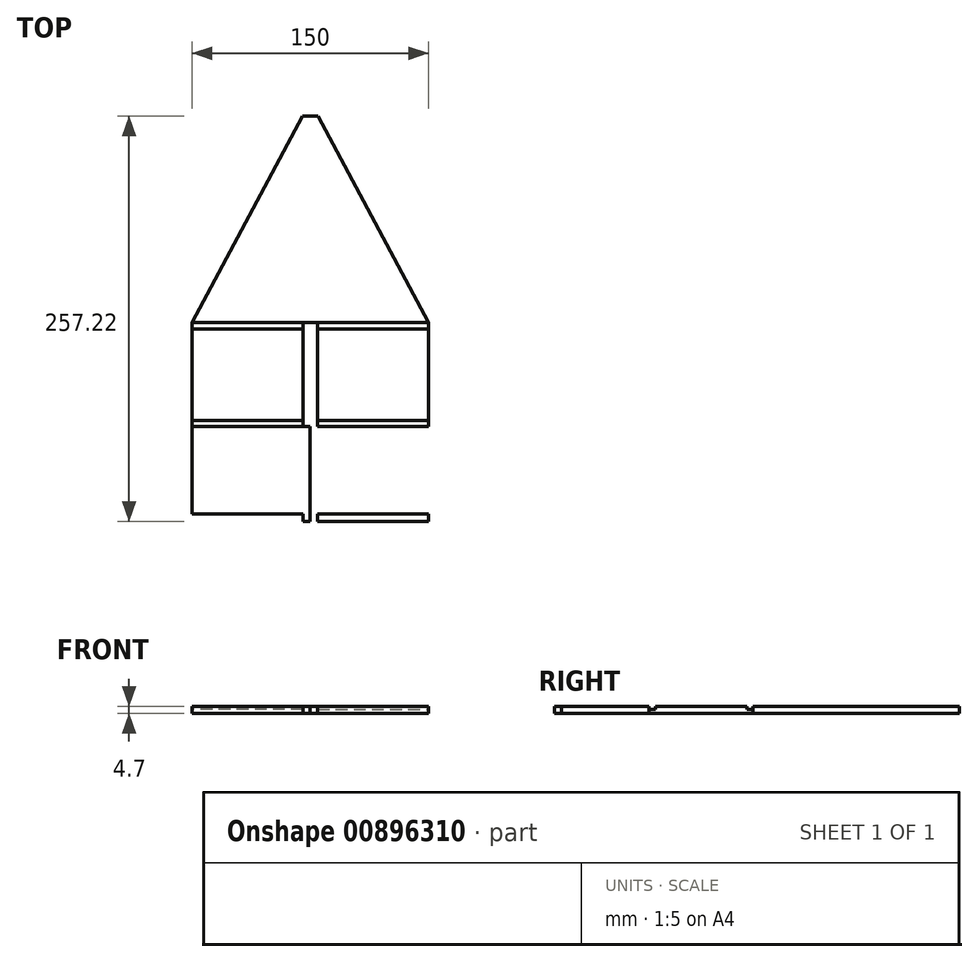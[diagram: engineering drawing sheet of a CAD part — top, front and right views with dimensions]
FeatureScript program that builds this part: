
annotation { "Feature Type Name" : "Feature", "Feature Type Description" : "" }
export const myFeature = defineFeature(function(context is Context, id is Id, definition is map)
    precondition{}
    {
        {
            var Q0;
            Q0=qCreatedBy(makeId("Top.planeOp"),FACE);
            var sketch = newSketch(context, id + "F0", { "sketchPlane" : qUnion([Q0])});
            skLineSegment(sketch, "E0", {"start": v(0, 0) * mm, "end": v(0, 135.77) * mm});
            skLineSegment(sketch, "E1", {"start": v(0, 0) * mm, "end": v(0, -124.23) * mm});
            skLineSegment(sketch, "E2", {"start": v(75, 0) * mm, "end": v(75, -124.23) * mm});
            skLineSegment(sketch, "E3", {"start": v(75, -124.23) * mm, "end": v(0, -124.23) * mm});
            skLineSegment(sketch, "E4.MirrorCS", {"start": v(-75, 0) * mm, "end": v(-75, -124.23) * mm});
            skLineSegment(sketch, "E5.left", {"start": v(-75, 2) * mm, "end": v(-75, -2) * mm});
            skLineSegment(sketch, "E5.right", {"start": v(0, 2) * mm, "end": v(0, -2) * mm});
            skPoint(sketch, "E5.middle", {"position": v(-37.5, 0) * mm});
            skLineSegment(sketch, "E6", {"start": v(75, -2) * mm, "end": v(75, 2) * mm});
            skLineSegment(sketch, "E7", {"start": v(-4.7, -2) * mm, "end": v(-75, -2) * mm});
            skLineSegment(sketch, "E8", {"start": v(-4.7, -2) * mm, "end": v(-4.7, 2) * mm});
            skLineSegment(sketch, "E9", {"start": v(-4.7, 2) * mm, "end": v(-75, 2) * mm});
            skLineSegment(sketch, "E10", {"start": v(4.7, 2) * mm, "end": v(4.7, -2) * mm});
            skLineSegment(sketch, "E11", {"start": v(4.7, 2) * mm, "end": v(75, 2) * mm});
            skLineSegment(sketch, "E12", {"start": v(4.7, -2) * mm, "end": v(75, -2) * mm});
            skLineSegment(sketch, "E13", {"start": v(0, -62.12) * mm, "end": v(0, -60.12) * mm});
            skLineSegment(sketch, "E14", {"start": v(0, -60.12) * mm, "end": v(0, -64.12) * mm});
            skLineSegment(sketch, "E15.left", {"start": v(0, -64.12) * mm, "end": v(0, -64.12) * mm});
            skLineSegment(sketch, "E15.right", {"start": v(-4.7, -64.12) * mm, "end": v(-4.7, -64.12) * mm});
            skLineSegment(sketch, "E16.bottom", {"start": v(-4.7, -64.12) * mm, "end": v(-75, -64.12) * mm});
            skLineSegment(sketch, "E16.top", {"start": v(-4.7, -60.12) * mm, "end": v(-75, -60.12) * mm});
            skLineSegment(sketch, "E16.left", {"start": v(-4.7, -64.12) * mm, "end": v(-4.7, -60.12) * mm});
            skLineSegment(sketch, "E16.right", {"start": v(-75, -64.12) * mm, "end": v(-75, -60.12) * mm});
            skLineSegment(sketch, "E17.bottom", {"start": v(75, -64.12) * mm, "end": v(4.7, -64.12) * mm});
            skLineSegment(sketch, "E17.top", {"start": v(75, -60.12) * mm, "end": v(4.7, -60.12) * mm});
            skLineSegment(sketch, "E17.left", {"start": v(75, -64.12) * mm, "end": v(75, -60.12) * mm});
            skLineSegment(sketch, "E17.right", {"start": v(4.7, -64.12) * mm, "end": v(4.7, -60.12) * mm});
            skLineSegment(sketch, "E18", {"start": v(0, 132.99) * mm, "end": v(4.9, 132.99) * mm});
            skLineSegment(sketch, "E19", {"start": v(4.9, 132.99) * mm, "end": v(-4.9, 132.99) * mm});
            skLineSegment(sketch, "E20", {"start": v(-75, 2) * mm, "end": v(-4.9, 132.99) * mm});
            skLineSegment(sketch, "E21", {"start": v(4.9, 132.99) * mm, "end": v(75, 2) * mm});
            skLineSegment(sketch, "E22.bottom", {"start": v(-4.7, 2) * mm, "end": v(4.7, 2) * mm});
            skLineSegment(sketch, "E22.top", {"start": v(-4.7, -64.12) * mm, "end": v(4.7, -64.12) * mm});
            skLineSegment(sketch, "E22.left", {"start": v(-4.7, 2) * mm, "end": v(-4.7, -64.12) * mm});
            skLineSegment(sketch, "E22.right", {"start": v(4.7, 2) * mm, "end": v(4.7, -64.12) * mm});
            skPoint(sketch, "E23", {"position": v(0, 67.88) * mm});
            skLineSegment(sketch, "E24", {"start": v(-75, -124.23) * mm, "end": v(-75, -119.53) * mm});
            skLineSegment(sketch, "E25", {"start": v(-4.7, -121.77) * mm, "end": v(-4.7, -119.53) * mm});
            skLineSegment(sketch, "E26", {"start": v(-4.7, -119.53) * mm, "end": v(-4.7, -124.23) * mm});
            skLineSegment(sketch, "E27", {"start": v(-75, -119.53) * mm, "end": v(-4.7, -119.53) * mm});
            skLineSegment(sketch, "E28", {"start": v(-4.7, -124.23) * mm, "end": v(-75, -124.23) * mm});
            skLineSegment(sketch, "E29", {"start": v(4.7, -124.23) * mm, "end": v(4.7, -119.53) * mm});
            skLineSegment(sketch, "E30", {"start": v(4.7, -119.53) * mm, "end": v(75, -119.53) * mm});
            skLineSegment(sketch, "E31", {"start": v(75, -119.53) * mm, "end": v(75, -124.23) * mm});
            skLineSegment(sketch, "E32", {"start": v(4.7, -124.23) * mm, "end": v(75, -124.23) * mm});
            skLineSegment(sketch, "E33", {"start": v(-4.7, -124.23) * mm, "end": v(0, -124.23) * mm});
            skSolve(sketch);
        }
        {
            var Q0;
            {var subQ0=sQuery(id+"F0.wireOp",EDGE,"NQw7m6NX-bP05-rJFs-aLFM-QvZ5EVc9hHf1");Q0=makeQuery(id+"F0.imprint","IMPRINT",FACE,{"disambiguationData":[TD([[makeQuery(id+"F0.imprint","IMPRINT",EDGE,{"derivedFrom":subQ0}),-1.0]])]});}
            var Q1;
            {var subQ0=sQuery(id+"F0.wireOp",EDGE,"F1fsQoGa-7jEL-UyxS-9MLj-w4imjhFZCvLi");Q1=makeQuery(id+"F0.imprint","IMPRINT",FACE,{"disambiguationData":[TD([[makeQuery(id+"F0.imprint","IMPRINT",EDGE,{"derivedFrom":subQ0}),1.0]])]});}
            var Q2;
            {var subQ0=sQuery(id+"F0.wireOp",EDGE,"bdf75b9f-238e-4a4f-a461-7d778147b3430.MirrorCS");Q2=makeQuery(id+"F0.imprint","IMPRINT",FACE,{"disambiguationData":[TD([[makeQuery(id+"F0.imprint","IMPRINT",EDGE,{"derivedFrom":subQ0}),1.0]])]});}
            var Q3;
            {var subQ0=sQuery(id+"F0.wireOp",EDGE,"E3");Q3=makeQuery(id+"F0.imprint","IMPRINT",FACE,{"disambiguationData":[TD([[makeQuery(id+"F0.imprint","IMPRINT",EDGE,{"derivedFrom":subQ0}),-1.0]])]});}
            var Q4;
            {var subQ2=sQuery(id+"F0.wireOp",EDGE,"qfcHIllW-OWiN-GYrw-DO88-jx2JwcBr6YpV");Q4=makeQuery(id+"F0.imprint","IMPRINT",FACE,{"disambiguationData":[TD([[makeQuery(id+"F0.imprint","IMPRINT",EDGE,{"derivedFrom":subQ2}),1.0]])]});}
            var Q5;
            {var subQ0=sQuery(id+"F0.wireOp",EDGE,"E5.top");Q5=makeQuery(id+"F0.imprint","IMPRINT",FACE,{"disambiguationData":[TD([[makeQuery(id+"F0.imprint","IMPRINT",EDGE,{"derivedFrom":subQ0}),-1.0]])]});}
            var Q6;
            {var subQ0=sQuery(id+"F0.wireOp",EDGE,"6iKSknnh-b4r3-sUiA-EbXK-GRWwRzz910pE");Q6=makeQuery(id+"F0.imprint","IMPRINT",FACE,{"disambiguationData":[TD([[makeQuery(id+"F0.imprint","IMPRINT",EDGE,{"derivedFrom":subQ0}),-1.0]])]});}
            var Q7;
            {var subQ3=sQuery(id+"F0.wireOp",EDGE,"E16.bottom");Q7=makeQuery(id+"F0.imprint","IMPRINT",FACE,{"disambiguationData":[TD([[makeQuery(id+"F0.imprint","IMPRINT",EDGE,{"derivedFrom":subQ3}),1.0]])]});}
            var Q8;
            {var subQ0=sQuery(id+"F0.wireOp",EDGE,"E7");Q8=makeQuery(id+"F0.imprint","IMPRINT",FACE,{"disambiguationData":[TD([[makeQuery(id+"F0.imprint","IMPRINT",EDGE,{"derivedFrom":subQ0}),1.0]])]});}
            var Q9;
            {var subQ0=sQuery(id+"F0.wireOp",EDGE,"E12");Q9=makeQuery(id+"F0.imprint","IMPRINT",FACE,{"disambiguationData":[TD([[makeQuery(id+"F0.imprint","IMPRINT",EDGE,{"derivedFrom":subQ0}),-1.0]])]});}
            var Q10;
            {var subQ4=sQuery(id+"F0.wireOp",EDGE,"E11");Q10=makeQuery(id+"F0.imprint","IMPRINT",FACE,{"disambiguationData":[TD([[makeQuery(id+"F0.imprint","IMPRINT",EDGE,{"derivedFrom":subQ4}),1.0]])]});}
            var Q11;
            {var subQ1=sQuery(id+"F0.wireOp",EDGE,"E9");Q11=makeQuery(id+"F0.imprint","IMPRINT",FACE,{"disambiguationData":[TD([[makeQuery(id+"F0.imprint","IMPRINT",EDGE,{"derivedFrom":subQ1}),-1.0]])]});}
            var Q12;
            {var subQ0=sQuery(id+"F0.wireOp",EDGE,"E5.right");var subQ3=makeQuery(id+"F0.imprint","IMPRINT",VERTEX,{"derivedFrom":subQ0});Q12=makeQuery(id+"F0.imprint","IMPRINT",FACE,{"disambiguationData":[TD([[makeQuery(id+"F0.imprint","IMPRINT",EDGE,{"disambiguationData":[TD([[subQ3,-1.0]])],"derivedFrom":subQ0}),-1.0]])]});}
            var Q13;
            {var subQ0=sQuery(id+"F0.wireOp",EDGE,"E5.right");var subQ3=makeQuery(id+"F0.imprint","IMPRINT",VERTEX,{"derivedFrom":subQ0});Q13=makeQuery(id+"F0.imprint","IMPRINT",FACE,{"disambiguationData":[TD([[makeQuery(id+"F0.imprint","IMPRINT",EDGE,{"disambiguationData":[TD([[subQ3,-1.0]])],"derivedFrom":subQ0}),1.0]])]});}
            extrude(context, id + "F1", {"entities" : qUnion([Q0, Q1, Q2, Q3, Q4, Q5, Q6, Q7, Q8, Q9, Q10, Q11, Q12, Q13]), "depth" : 4.7 * mm, "offsetDistance" : 25 * mm});
        }
        {
            var Q0;
            {var subQ0=sQuery(id+"F0.wireOp",EDGE,"E7");Q0=makeQuery(id+"F0.imprint","IMPRINT",FACE,{"disambiguationData":[TD([[makeQuery(id+"F0.imprint","IMPRINT",EDGE,{"derivedFrom":subQ0}),-1.0]])]});}
            var Q1;
            Q1=makeQuery(id+"F0.imprint","IMPRINT",FACE,{"disambiguationData":[TD([[makeQuery(id+"F0.imprint","IMPRINT",EDGE,{"derivedFrom":sQuery(id+"F0.wireOp",EDGE,"E10")}),1.0]])]});
            extrude(context, id + "F2", {"entities" : qUnion([Q0, Q1]), "operationType" : NewBodyOperationType.ADD, "depth" : 2.7 * mm, "offsetDistance" : 25 * mm});
        }
        {
            var Q0;
            Q0=makeQuery(id+"F0.imprint","IMPRINT",FACE,{"disambiguationData":[TD([[makeQuery(id+"F0.imprint","IMPRINT",EDGE,{"derivedFrom":sQuery(id+"F0.wireOp",EDGE,"E16.bottom")}),-1.0]])]});
            var Q1;
            Q1=makeQuery(id+"F0.imprint","IMPRINT",FACE,{"disambiguationData":[TD([[makeQuery(id+"F0.imprint","IMPRINT",EDGE,{"derivedFrom":sQuery(id+"F0.wireOp",EDGE,"E17.bottom")}),-1.0]])]});
            var Q2;
            {var subQ2=sQuery(id+"F0.wireOp",EDGE,"E11");Q2=makeQuery(id+"F0.imprint","IMPRINT",FACE,{"disambiguationData":[TD([[makeQuery(id+"F0.imprint","IMPRINT",EDGE,{"derivedFrom":subQ2}),-1.0]])]});}
            var Q3;
            Q3=makeQuery(id+"F0.imprint","IMPRINT",FACE,{"disambiguationData":[TD([[makeQuery(id+"F0.imprint","IMPRINT",EDGE,{"derivedFrom":sQuery(id+"F0.wireOp",EDGE,"E24")}),-1.0]])]});
            var Q4;
            Q4=makeQuery(id+"F0.imprint","IMPRINT",FACE,{"disambiguationData":[TD([[makeQuery(id+"F0.imprint","IMPRINT",EDGE,{"derivedFrom":sQuery(id+"F0.wireOp",EDGE,"E29")}),-1.0]])]});
            extrude(context, id + "F3", {"entities" : qUnion([Q0, Q1, Q2, Q3, Q4]), "operationType" : NewBodyOperationType.ADD, "depth" : 2.7 * mm, "offsetDistance" : 25 * mm});
        }
    });
